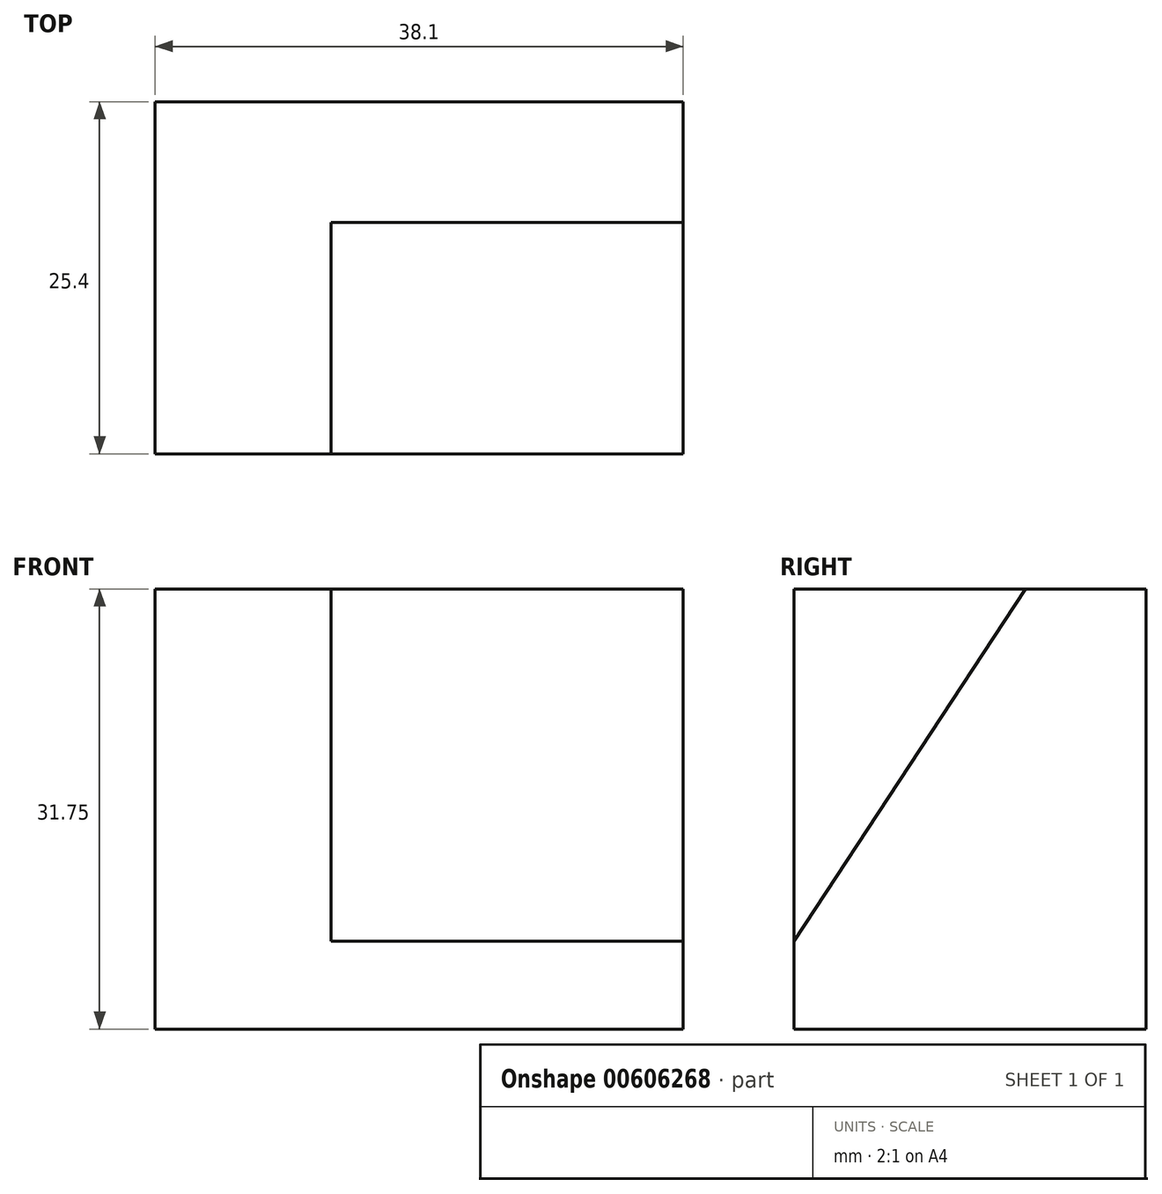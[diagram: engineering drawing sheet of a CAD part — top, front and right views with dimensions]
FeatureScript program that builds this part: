
annotation { "Feature Type Name" : "Feature", "Feature Type Description" : "" }
export const myFeature = defineFeature(function(context is Context, id is Id, definition is map)
    precondition{}
    {
        {
            var Q0;
            Q0=qCreatedBy(makeId("Right.planeOp"),FACE);
            var sketch = newSketch(context, id + "F0", { "sketchPlane" : qUnion([Q0])});
            skLineSegment(sketch, "E0", {"start": v(0, 0) * mm, "end": v(25.4, 0) * mm});
            skLineSegment(sketch, "E1", {"start": v(0, 0) * mm, "end": v(0, 31.75) * mm});
            skLineSegment(sketch, "E2", {"start": v(25.4, 0) * mm, "end": v(25.4, 31.75) * mm});
            skLineSegment(sketch, "E3", {"start": v(0, 31.75) * mm, "end": v(25.4, 31.75) * mm});
            skSolve(sketch);
        }
        {
            var Q0;
            Q0=makeQuery(id+"F0.imprint","IMPRINT",FACE,{"disambiguationData":[TD([[makeQuery(id+"F0.imprint","IMPRINT",EDGE,{"derivedFrom":sQuery(id+"F0.wireOp",EDGE,"E0")}),1.0]])]});
            extrude(context, id + "F1", {"entities" : qUnion([Q0]), "depth" : 38.1 * mm, "offsetDistance" : 25.4 * mm});
        }
        {
            var Q0;
            Q0=makeQuery(id+"F1.opExtrude","CAP_FACE",FACE,{"disambiguationData":[OSD([sQuery(id+"F0.wireOp",EDGE,"E0"),sQuery(id+"F0.wireOp",EDGE,"E1"),sQuery(id+"F0.wireOp",EDGE,"E2"),sQuery(id+"F0.wireOp",EDGE,"E3")])],"isStart":false});
            var sketch = newSketch(context, id + "F2", { "sketchPlane" : qUnion([Q0])});
            skLineSegment(sketch, "E4", {"start": v(0, 0) * mm, "end": v(0, 6.35) * mm});
            skLineSegment(sketch, "E5", {"start": v(0, 6.35) * mm, "end": v(0, 31.75) * mm});
            skLineSegment(sketch, "E6", {"start": v(0, 31.75) * mm, "end": v(16.7, 31.75) * mm});
            skLineSegment(sketch, "E7", {"start": v(16.7, 31.75) * mm, "end": v(0, 6.35) * mm});
            skSolve(sketch);
        }
        {
            var Q0;
            Q0=makeQuery(id+"F2.imprint","IMPRINT",FACE,{"disambiguationData":[TD([[makeQuery(id+"F2.imprint","IMPRINT",EDGE,{"derivedFrom":sQuery(id+"F2.wireOp",EDGE,"E5")}),-1.0]])]});
            extrude(context, id + "F3", {"entities" : qUnion([Q0]), "operationType" : NewBodyOperationType.REMOVE, "oppositeDirection" : true, "depth" : 25.4 * mm, "offsetDistance" : 25.4 * mm});
        }
    });
